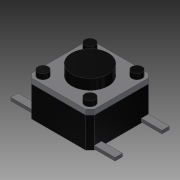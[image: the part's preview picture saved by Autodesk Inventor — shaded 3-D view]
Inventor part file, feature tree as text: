
AUTODESK INVENTOR PART (.ipt)
format: ipt  version: 2015 (Build 190159000, 159)  size: 236,032 bytes
history: native  units: mm
features: extrude x10, sketch x8, projected_geometry x3, mirror x2, other x1, plane x1
ambient origin geometry x8: Origin, YZ Plane, XZ Plane, XY Plane, X Axis, Y Axis, Z Axis, Center Point
bodies: Body1 (feature_tree)
feature tree (25):
  other  "Sólido1"
  sketch  "Boceto1"  dims[d0=6.0mm d1=6.0mm]
  extrude  "Extrusión1"  Depth=6.0mm
  extrude  "Extrusión2"  Depth=4.5mm
  extrude  "Extrusión3"  Depth=3.5mm
  plane  "Plano de trabajo1"
  extrude  "Extrusión4"  Depth=0.4mm
  extrude  "Extrusión5"  Depth=0.4mm
  mirror  "Simetría1"
  extrude  "Extrusión6"  Depth=0.4mm
  mirror  "Simetría2"
  extrude  "Extrusión7"  Depth=0.4mm
  extrude  "Extrusión8"  Depth=0.5mm TaperAngle=0.0deg
  extrude  "Extrusión9"  Depth=1.0mm TaperAngle=0.0deg
  extrude  "Extrusión10"  [1 undecoded]
  sketch  "Boceto2"  dims[d2=4.5mm d4=4.5mm]
  projected_geometry  "Contorno proyectado1"
  sketch  "Boceto3"  dims[d5=1.0mm d6=3.5mm]
  projected_geometry  "Contorno proyectado2"
  sketch  "Boceto4"  dims[d7=0.4mm d8=0.4mm]
  projected_geometry  "Contorno proyectado3"
  sketch  "Boceto5"  dims[d9=0.4mm d10=0.4mm]
  sketch  "Boceto6"  dims[d11=0.4mm d12=0.4mm]
  sketch  "Boceto7"  dims[d13=0.4mm d14=0.4mm]
  sketch  "Boceto8"  dims[d15=3.4mm d16=0.0mm d17=0.5mm d18=0.0mm d19=1.0mm d20=0.0mm d21=-3.0mm d22=2.0mm d23=0.7mm d24=0.75mm d25=20.0mm d27=4.5mm d28=20.0mm d30=8.0mm d33=0.3mm d34=0.0mm d35=0.5mm d36=0.0001mm d37=0.0mm d38=0.5mm d39=0.0001mm d40=0.0mm d41=0.0001mm d42=0.0mm d43=0.0001mm d44=0.0mm d45=0.0001mm d46=0.0mm d47=0.0001mm d48=0.0mm]
note: 1 required parameter value undecoded (feature->parameter linkage not recoverable at this tier; creation-order binding heuristic only, values carry confidence <= 0.55)
